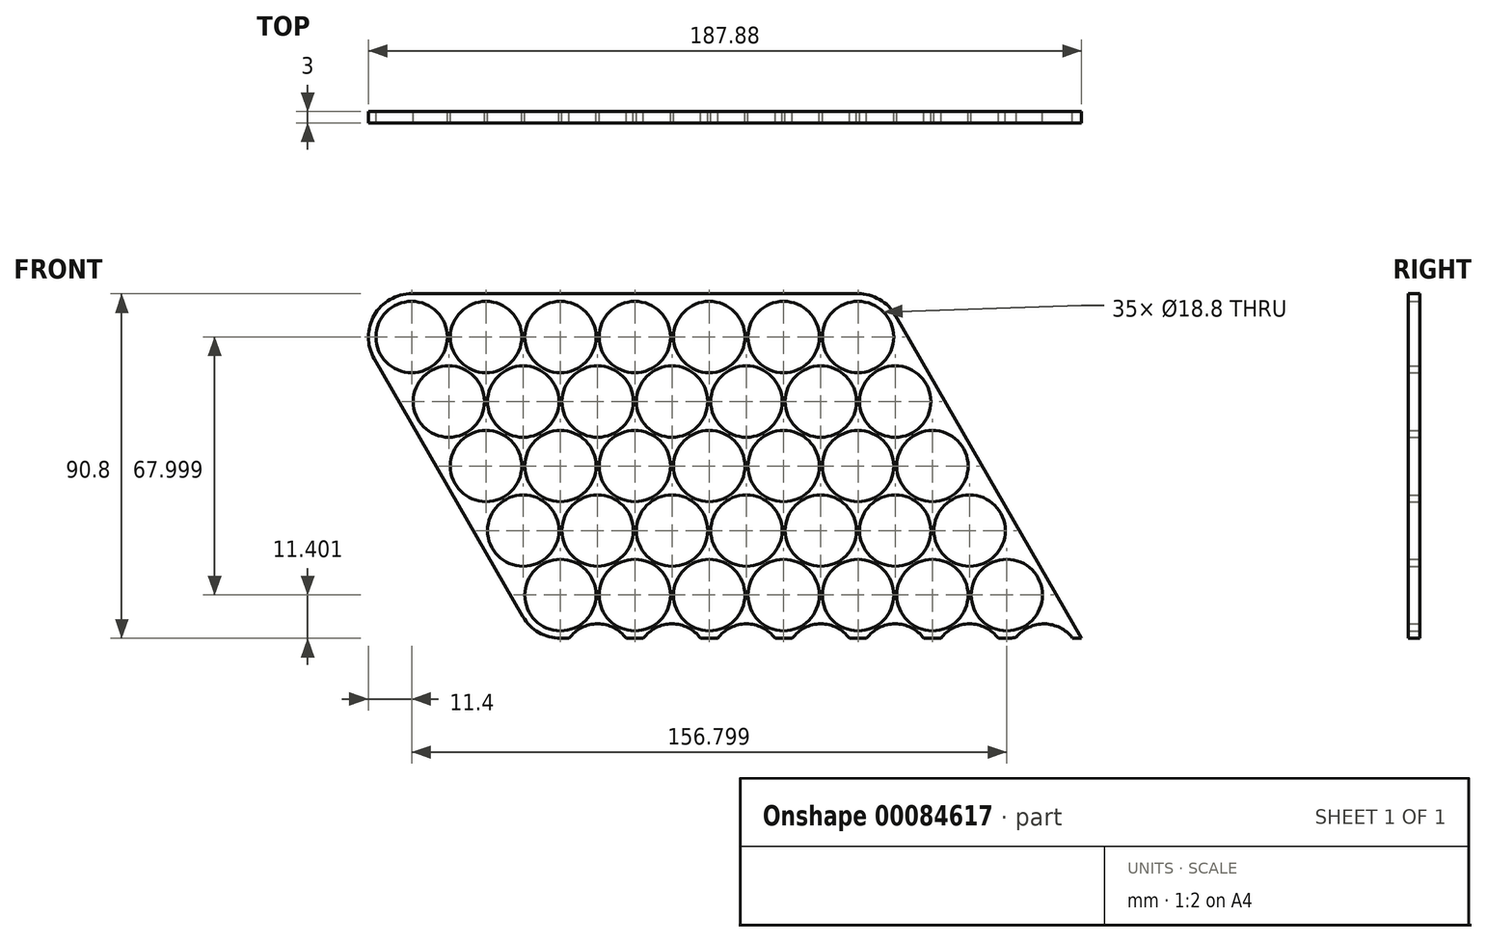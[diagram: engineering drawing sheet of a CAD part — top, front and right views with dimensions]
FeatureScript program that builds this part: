
annotation { "Feature Type Name" : "Feature", "Feature Type Description" : "" }
export const myFeature = defineFeature(function(context is Context, id is Id, definition is map)
    precondition{}
    {
        {
            var Q0;
            Q0=qCreatedBy(makeId("Front.planeOp"),FACE);
            var sketch = newSketch(context, id + "F0", { "sketchPlane" : qUnion([Q0]) });
            skCircle(sketch, "E0", {"center": v(0, 0) * mm, "radius": 9.4 * mm});
            skCircle(sketch, "E1.1.0.0", {"center": v(19.6, 0) * mm, "radius": 9.4 * mm});
            skCircle(sketch, "E1.2.0.0", {"center": v(39.2, 0) * mm, "radius": 9.4 * mm});
            skCircle(sketch, "E1.3.0.0", {"center": v(58.8, 0) * mm, "radius": 9.4 * mm});
            skLineSegment(sketch, "E1.direction1", {"start": v(0, 0) * mm, "end": v(19.6, 0) * mm, "construction": true});
            skLineSegment(sketch, "E2", {"start": v(0, -17) * mm, "end": v(73.2, -17) * mm, "construction": true});
            skLineSegment(sketch, "E3", {"start": v(9.8, 0) * mm, "end": v(9.8, -17) * mm, "construction": true});
            skCircle(sketch, "E4", {"center": v(9.8, -17) * mm, "radius": 9.4 * mm});
            skCircle(sketch, "E5.1.0.0", {"center": v(29.4, -17) * mm, "radius": 9.4 * mm});
            skCircle(sketch, "E5.2.0.0", {"center": v(49, -17) * mm, "radius": 9.4 * mm});
            skCircle(sketch, "E5.3.0.0", {"center": v(68.6, -17) * mm, "radius": 9.4 * mm});
            skLineSegment(sketch, "E5.direction1", {"start": v(9.8, -17) * mm, "end": v(29.4, -17) * mm, "construction": true});
            skLineSegment(sketch, "E6", {"start": v(-8.14, -4.7) * mm, "end": v(1.66, -21.7) * mm});
            skLineSegment(sketch, "E7", {"start": v(0, 9.4) * mm, "end": v(58.8, 9.4) * mm});
            skLineSegment(sketch, "E8", {"start": v(9.8, -17) * mm, "end": v(9.8, -26.4) * mm, "construction": true});
            skLineSegment(sketch, "E9", {"start": v(68.6, -17) * mm, "end": v(68.6, -26.4) * mm, "construction": true});
            skArc(sketch, "E10", {"start": v(58.8, 9.4) * mm, "mid": v(63.5, 8.14) * mm, "end": v(66.94, 4.7) * mm});
            skArc(sketch, "E11", {"start": v(76.74, -12.3) * mm, "mid": v(76.74, -21.7) * mm, "end": v(68.6, -26.4) * mm});
            skArc(sketch, "E12", {"start": v(9.8, -26.4) * mm, "mid": v(5.1, -25.14) * mm, "end": v(1.66, -21.7) * mm});
            skArc(sketch, "E13", {"start": v(-8.14, -4.7) * mm, "mid": v(-8.14, 4.7) * mm, "end": v(0, 9.4) * mm});
            skArc(sketch, "E14.0", {"start": v(0, 11.4) * mm, "mid": v(-9.87, 5.7) * mm, "end": v(-9.88, -5.7) * mm});
            skLineSegment(sketch, "E15.0", {"start": v(0, 11.4) * mm, "end": v(58.8, 11.4) * mm});
            skLineSegment(sketch, "E16.0", {"start": v(-9.88, -5.7) * mm, "end": v(-0.08, -22.7) * mm});
            skArc(sketch, "E17.trimOffspring", {"start": v(9.8, -5.82) * mm, "mid": v(9.87, -5.71) * mm, "end": v(9.93, -5.6) * mm});
            skArc(sketch, "E18.trimOffspring", {"start": v(9.93, -5.6) * mm, "mid": v(9.86, -5.6) * mm, "end": v(9.8, -5.6) * mm});
            skCircle(sketch, "E19.0.4.0", {"center": v(78.4, 0) * mm, "radius": 9.4 * mm});
            skCircle(sketch, "E19.0.5.0", {"center": v(98, 0) * mm, "radius": 9.4 * mm});
            skCircle(sketch, "E20.0.4.0", {"center": v(88.2, -17) * mm, "radius": 9.4 * mm});
            skCircle(sketch, "E20.0.5.0", {"center": v(107.8, -17) * mm, "radius": 9.4 * mm});
            skLineSegment(sketch, "E21", {"start": v(58.8, 11.4) * mm, "end": v(98, 11.4) * mm});
            skLineSegment(sketch, "E22", {"start": v(0, 0) * mm, "end": v(9.8, -17) * mm, "construction": true});
            skCircle(sketch, "E23.1.0.0", {"center": v(19.6, -34) * mm, "radius": 9.4 * mm});
            skCircle(sketch, "E23.2.0.0", {"center": v(29.4, -51) * mm, "radius": 9.4 * mm});
            skLineSegment(sketch, "E23.direction1", {"start": v(9.8, -17) * mm, "end": v(19.6, -34) * mm, "construction": true});
            skCircle(sketch, "E24.1.0.0", {"center": v(39.2, -34) * mm, "radius": 9.4 * mm});
            skCircle(sketch, "E24.1.0.1", {"center": v(49, -51) * mm, "radius": 9.4 * mm});
            skCircle(sketch, "E24.2.0.0", {"center": v(58.8, -34) * mm, "radius": 9.4 * mm});
            skCircle(sketch, "E24.2.0.1", {"center": v(68.6, -51) * mm, "radius": 9.4 * mm});
            skCircle(sketch, "E24.3.0.0", {"center": v(78.4, -34) * mm, "radius": 9.4 * mm});
            skCircle(sketch, "E24.3.0.1", {"center": v(88.2, -51) * mm, "radius": 9.4 * mm});
            skCircle(sketch, "E24.4.0.0", {"center": v(98, -34) * mm, "radius": 9.4 * mm});
            skCircle(sketch, "E24.4.0.1", {"center": v(107.8, -51) * mm, "radius": 9.4 * mm});
            skCircle(sketch, "E24.5.0.0", {"center": v(117.6, -34) * mm, "radius": 9.4 * mm});
            skCircle(sketch, "E24.5.0.1", {"center": v(127.4, -51) * mm, "radius": 9.4 * mm});
            skLineSegment(sketch, "E24.direction1", {"start": v(19.6, -34) * mm, "end": v(39.2, -34) * mm, "construction": true});
            skLineSegment(sketch, "E25", {"start": v(-0.08, -22.7) * mm, "end": v(19.52, -56.7) * mm});
            skArc(sketch, "E26.0", {"start": v(29.27, -62.4) * mm, "mid": v(29.33, -62.4) * mm, "end": v(29.4, -62.4) * mm});
            skCircle(sketch, "E27.0.6.0", {"center": v(117.6, 0) * mm, "radius": 9.4 * mm});
            skCircle(sketch, "E28.0.6.0", {"center": v(127.4, -17) * mm, "radius": 9.4 * mm});
            skCircle(sketch, "E29.0.6.0", {"center": v(137.2, -34) * mm, "radius": 9.4 * mm});
            skCircle(sketch, "E29.2.6.0", {"center": v(147, -51) * mm, "radius": 9.4 * mm});
            skLineSegment(sketch, "E30", {"start": v(98, 11.4) * mm, "end": v(117.6, 11.4) * mm});
            skCircle(sketch, "E31.0.3.0", {"center": v(39.2, -68) * mm, "radius": 9.4 * mm});
            skCircle(sketch, "E32.1.0.0", {"center": v(58.8, -68) * mm, "radius": 9.4 * mm});
            skCircle(sketch, "E32.2.0.0", {"center": v(78.4, -68) * mm, "radius": 9.4 * mm});
            skCircle(sketch, "E32.3.0.0", {"center": v(98, -68) * mm, "radius": 9.4 * mm});
            skCircle(sketch, "E32.4.0.0", {"center": v(117.6, -68) * mm, "radius": 9.4 * mm});
            skCircle(sketch, "E32.5.0.0", {"center": v(137.2, -68) * mm, "radius": 9.4 * mm});
            skCircle(sketch, "E32.6.0.0", {"center": v(156.8, -68) * mm, "radius": 9.4 * mm});
            skLineSegment(sketch, "E32.direction1", {"start": v(39.2, -68) * mm, "end": v(58.8, -68) * mm, "construction": true});
            skArc(sketch, "E33.0", {"start": v(29.32, -73.7) * mm, "mid": v(33.5, -77.87) * mm, "end": v(39.2, -79.4) * mm});
            skLineSegment(sketch, "E34", {"start": v(19.52, -56.7) * mm, "end": v(29.32, -73.7) * mm});
            skLineSegment(sketch, "E35", {"start": v(39.2, -79.4) * mm, "end": v(41.45, -79.4) * mm});
            skArc(sketch, "E36", {"start": v(127.48, 5.7) * mm, "mid": v(123.3, 9.87) * mm, "end": v(117.6, 11.4) * mm});
            skArc(sketch, "E37", {"start": v(156.8, -79.4) * mm, "mid": v(158.03, -79.33) * mm, "end": v(159.26, -79.13) * mm});
            skLineSegment(sketch, "E38", {"start": v(127.48, 5.7) * mm, "end": v(166.68, -62.3) * mm});
            skArc(sketch, "E39.0.4.0", {"start": v(56.55, -79.4) * mm, "mid": v(49, -75.6) * mm, "end": v(41.45, -79.4) * mm});
            skArc(sketch, "E40.1.0.0", {"start": v(76.15, -79.4) * mm, "mid": v(68.6, -75.6) * mm, "end": v(61.05, -79.4) * mm});
            skArc(sketch, "E40.2.0.0", {"start": v(95.75, -79.4) * mm, "mid": v(88.2, -75.6) * mm, "end": v(80.65, -79.4) * mm});
            skArc(sketch, "E40.3.0.0", {"start": v(115.35, -79.4) * mm, "mid": v(107.8, -75.6) * mm, "end": v(100.25, -79.4) * mm});
            skArc(sketch, "E40.4.0.0", {"start": v(134.95, -79.4) * mm, "mid": v(127.4, -75.6) * mm, "end": v(119.85, -79.4) * mm});
            skArc(sketch, "E40.5.0.0", {"start": v(154.55, -79.4) * mm, "mid": v(147, -75.6) * mm, "end": v(139.45, -79.4) * mm});
            skArc(sketch, "E40.6.0.0", {"start": v(165.2, -75.7) * mm, "mid": v(161.9, -76.85) * mm, "end": v(159.26, -79.13) * mm});
            skLineSegment(sketch, "E40.direction1", {"start": v(49, -85) * mm, "end": v(68.6, -85) * mm, "construction": true});
            skLineSegment(sketch, "E41.trimOffspring", {"start": v(154.55, -79.4) * mm, "end": v(156.8, -79.4) * mm});
            skLineSegment(sketch, "E42.trimOffspring", {"start": v(134.95, -79.4) * mm, "end": v(139.45, -79.4) * mm});
            skLineSegment(sketch, "E43.trimOffspring", {"start": v(115.35, -79.4) * mm, "end": v(119.85, -79.4) * mm});
            skLineSegment(sketch, "E44.trimOffspring", {"start": v(95.75, -79.4) * mm, "end": v(100.25, -79.4) * mm});
            skLineSegment(sketch, "E45.trimOffspring", {"start": v(76.15, -79.4) * mm, "end": v(80.65, -79.4) * mm});
            skLineSegment(sketch, "E46.trimOffspring", {"start": v(56.55, -79.4) * mm, "end": v(61.05, -79.4) * mm});
            skArc(sketch, "E47", {"start": v(174.08, -79.3) * mm, "mid": v(166.7, -75.6) * mm, "end": v(159.26, -79.13) * mm});
            skLineSegment(sketch, "E48", {"start": v(166.68, -62.3) * mm, "end": v(176.48, -79.3) * mm});
            skLineSegment(sketch, "E49", {"start": v(156.8, -68) * mm, "end": v(166.6, -85) * mm, "construction": true});
            skLineSegment(sketch, "E50", {"start": v(166.6, -85) * mm, "end": v(185.3, -117.44) * mm, "construction": true});
            skLineSegment(sketch, "E51", {"start": v(176.48, -79.3) * mm, "end": v(174.08, -79.3) * mm});
            skSolve(sketch);
        }
        {
            var Q0;
            Q0=qSketchRegion(id+"F0",true);
            var Q1;
            {var subQ3=sQuery(id+"F0.wireOp",EDGE,"E1.1.0.0");Q1=makeQuery(id+"F0.imprint","IMPRINT",FACE,{"disambiguationData":[TD([[makeQuery(id+"F0.imprint","IMPRINT",EDGE,{"derivedFrom":subQ3}),-1.0]])]});}
            extrude(context, id + "F1", {"entities" : qUnion([Q0, Q1]), "depth" : 3 * mm});
        }
    });
